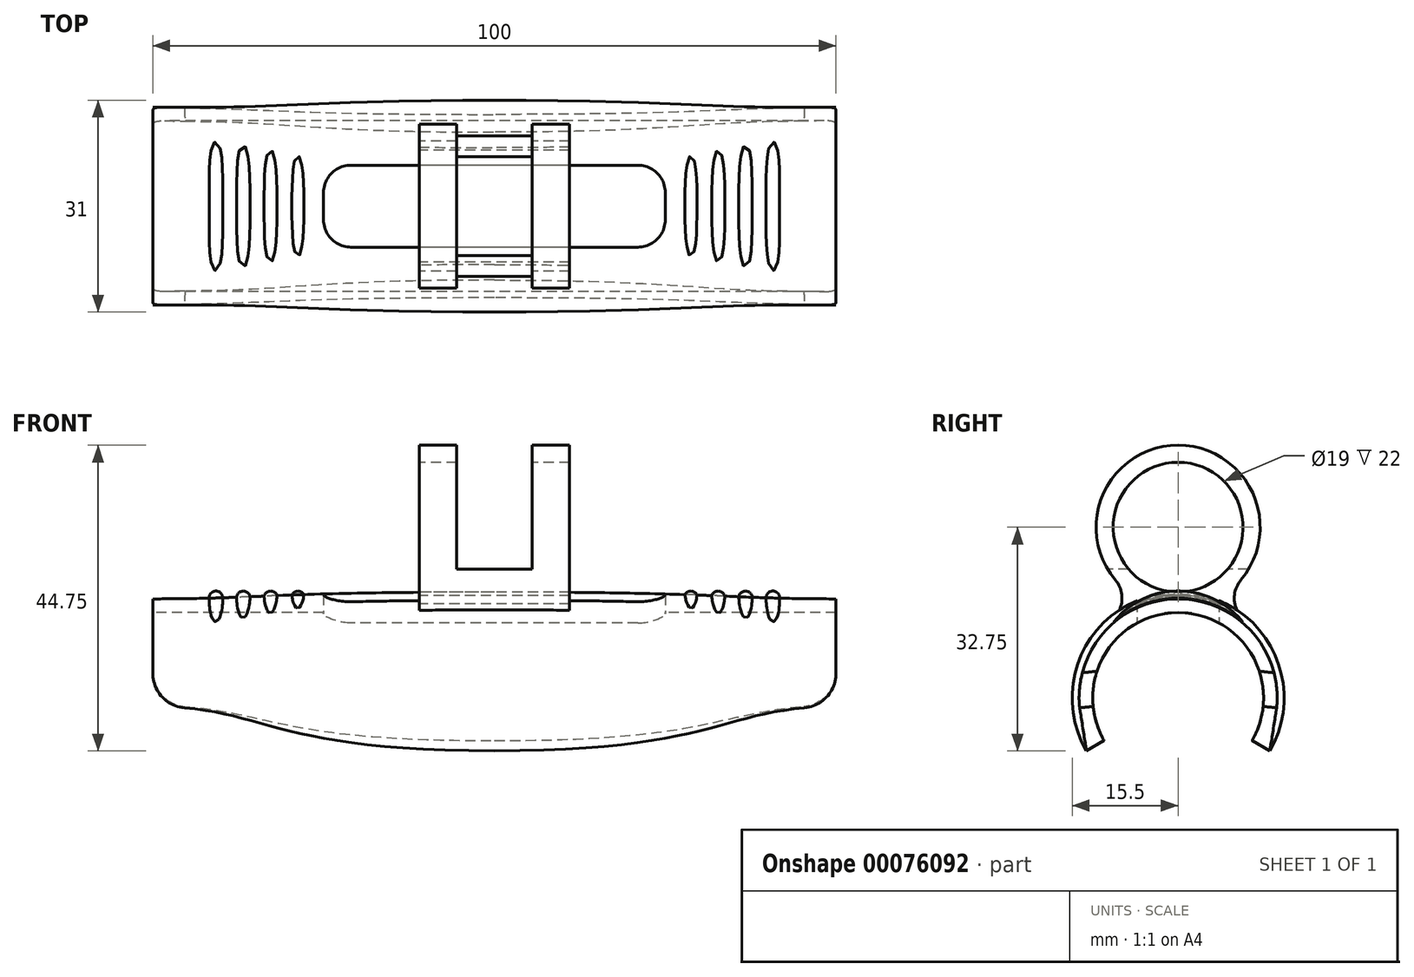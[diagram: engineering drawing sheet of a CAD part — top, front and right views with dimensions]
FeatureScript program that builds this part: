
annotation { "Feature Type Name" : "Feature", "Feature Type Description" : "" }
export const myFeature = defineFeature(function(context is Context, id is Id, definition is map)
    precondition{}
    {
        {
            var Q0;
            Q0=qCreatedBy(makeId("Right.planeOp"),FACE);
            var sketch = newSketch(context, id + "F0", { "sketchPlane" : qUnion([Q0])});
            skCircle(sketch, "E0", {"center": v(0, 0) * mm, "radius": 12.5 * mm});
            skSolve(sketch);
        }
        {
            var Q0;
            Q0=qCreatedBy(makeId("Right.planeOp"),FACE);
            var sketch = newSketch(context, id + "F1", { "sketchPlane" : qUnion([Q0])});
            skArc(sketch, "E1", {"start": v(10.83, -6.25) * mm, "mid": v(0, 12.5) * mm, "end": v(-10.83, -6.25) * mm});
            skArc(sketch, "E2.0", {"start": v(13.42, -7.75) * mm, "mid": v(0, 15.5) * mm, "end": v(-13.42, -7.75) * mm});
            skLineSegment(sketch, "E3", {"start": v(-10.83, -6.25) * mm, "end": v(-13.42, -7.75) * mm});
            skLineSegment(sketch, "E4", {"start": v(10.83, -6.25) * mm, "end": v(13.42, -7.75) * mm});
            skLineSegment(sketch, "E5", {"start": v(0, 20.1) * mm, "end": v(0, -26.2) * mm, "construction": true});
            skSolve(sketch);
        }
        {
            var Q0;
            Q0=qCreatedBy(makeId("Right.planeOp"),FACE);
            cPlane(context, id + "F2", {"entities" : qUnion([Q0]), "cplaneType" : CPlaneType.OFFSET, "offset" : 50 * mm, "width" : 152.4 * mm, "height" : 152.4 * mm});
        }
        {
            var Q0;
            Q0=qCreatedBy(id+"F2.planeOp",FACE);
            var sketch = newSketch(context, id + "F3", { "sketchPlane" : qUnion([Q0])});
            skArc(sketch, "E6", {"start": v(12.45, -1.09) * mm, "mid": v(0, 12.5) * mm, "end": v(-12.45, -1.09) * mm});
            skArc(sketch, "E7.0", {"start": v(14.44, -1.26) * mm, "mid": v(0, 14.5) * mm, "end": v(-14.44, -1.26) * mm});
            skLineSegment(sketch, "E8", {"start": v(-12.45, -1.09) * mm, "end": v(-14.44, -1.26) * mm});
            skLineSegment(sketch, "E9", {"start": v(12.45, -1.09) * mm, "end": v(14.44, -1.26) * mm});
            skSolve(sketch);
        }
        {
            var Q0;
            Q0=makeQuery(id+"F3.imprint","IMPRINT",FACE,{"disambiguationData":[TD([[makeQuery(id+"F3.imprint","IMPRINT",EDGE,{"derivedFrom":sQuery(id+"F3.wireOp",EDGE,"E6")}),-1.0]])]});
            var Q1;
            Q1 = qSketchRegion(id + "F1", true);
            loft(context, id + "F4", {"startCondition" : LoftEndDerivativeType.NORMAL_TO_PROFILE, "startMagnitude" : 1, "endCondition" : LoftEndDerivativeType.NORMAL_TO_PROFILE, "endMagnitude" : 2, "sheetProfilesArray" : [{ "sheetProfileEntities" : qUnion([Q0]) }, { "sheetProfileEntities" : qUnion([Q1]) }]});
        }
        {
            var Q0;
            Q0=makeQuery(id+"F4.opLoft","MID_CAP_EDGE",EDGE,{"disambiguationData":[OSD([sQuery(id+"F3.wireOp",EDGE,"E6"),sQuery(id+"F3.wireOp",EDGE,"E7.0"),sQuery(id+"F3.wireOp",EDGE,"E8")])],"capPos":0.0});
            var Q1;
            Q1=makeQuery(id+"F4.opLoft","MID_CAP_EDGE",EDGE,{"disambiguationData":[OSD([sQuery(id+"F3.wireOp",EDGE,"E6"),sQuery(id+"F3.wireOp",EDGE,"E7.0"),sQuery(id+"F3.wireOp",EDGE,"E9")])],"capPos":0.0});
            fillet(context, id + "F5", {"entities" : qUnion([Q0, Q1]), "radius" : 5.08 * mm, "tangentPropagation" : true, "allowEdgeOverflow" : false});
        }
        {
            var Q0;
            Q0=qCreatedBy(makeId("Top.planeOp"),FACE);
            var sketch = newSketch(context, id + "F6", { "sketchPlane" : qUnion([Q0])});
            skLineSegment(sketch, "E10.bottom", {"start": v(21, 6) * mm, "end": v(-25, 6) * mm});
            skLineSegment(sketch, "E10.top", {"start": v(21, -6) * mm, "end": v(-25, -6) * mm});
            skLineSegment(sketch, "E10.left", {"start": v(25, 2) * mm, "end": v(25, -2) * mm});
            skLineSegment(sketch, "E10.right", {"start": v(-25, 6) * mm, "end": v(-25, -6) * mm});
            skPoint(sketch, "E10.middle", {"position": v(0, 0) * mm});
            skPoint(sketch, "E11.visualSharp", {"position": v(25, 6) * mm});
            skArc(sketch, "E11.filletArc", {"start": v(25, 2) * mm, "mid": v(23.83, 4.83) * mm, "end": v(21, 6) * mm});
            skPoint(sketch, "E12.visualSharp", {"position": v(25, -6) * mm});
            skArc(sketch, "E12.filletArc", {"start": v(21, -6) * mm, "mid": v(23.83, -4.83) * mm, "end": v(25, -2) * mm});
            skSolve(sketch);
        }
        {
            var Q0;
            Q0=makeQuery(id+"F6.imprint","IMPRINT",FACE,{"disambiguationData":[TD([[makeQuery(id+"F6.imprint","IMPRINT",EDGE,{"derivedFrom":sQuery(id+"F6.wireOp",EDGE,"E10.bottom")}),1.0]])]});
            extrude(context, id + "F7", {"entities" : qUnion([Q0]), "operationType" : NewBodyOperationType.REMOVE, "depth" : 38.64 * mm});
        }
        {
            var Q0;
            Q0=qCreatedBy(makeId("Right.planeOp"),FACE);
            var sketch = newSketch(context, id + "F8", { "sketchPlane" : qUnion([Q0])});
            skArc(sketch, "E13", {"start": v(9.19, 17.28) * mm, "mid": v(0, 37) * mm, "end": v(-9.19, 17.28) * mm});
            skArc(sketch, "E14", {"start": v(9.68, 11.46) * mm, "mid": v(0, 15) * mm, "end": v(-9.68, 11.46) * mm});
            skArc(sketch, "E15", {"start": v(9.19, 17.28) * mm, "mid": v(8.23, 14.26) * mm, "end": v(9.68, 11.46) * mm});
            skArc(sketch, "E16", {"start": v(-9.68, 11.46) * mm, "mid": v(-8.23, 14.26) * mm, "end": v(-9.19, 17.28) * mm});
            skCircle(sketch, "E17", {"center": v(0, 25) * mm, "radius": 9.5 * mm});
            skSolve(sketch);
        }
        {
            var Q0;
            Q0=makeQuery(id+"F8.imprint","IMPRINT",FACE,{"disambiguationData":[TD([[makeQuery(id+"F8.imprint","IMPRINT",EDGE,{"derivedFrom":sQuery(id+"F8.wireOp",EDGE,"E13")}),1.0]])]});
            extrude(context, id + "F9", {"entities" : qUnion([Q0]), "operationType" : NewBodyOperationType.ADD, "depth" : 11 * mm});
        }
        {
            var Q0;
            Q0=qCreatedBy(makeId("Front.planeOp"),FACE);
            var sketch = newSketch(context, id + "F10", { "sketchPlane" : qUnion([Q0])});
            skCircle(sketch, "E18", {"center": v(28.75, 14.65) * mm, "radius": 1 * mm});
            skCircle(sketch, "E19.1.0.0", {"center": v(32.75, 14.65) * mm, "radius": 1 * mm});
            skCircle(sketch, "E19.2.0.0", {"center": v(36.75, 14.65) * mm, "radius": 1 * mm});
            skCircle(sketch, "E19.3.0.0", {"center": v(40.75, 14.65) * mm, "radius": 1 * mm});
            skLineSegment(sketch, "E19.direction1", {"start": v(28.75, 14.65) * mm, "end": v(32.75, 14.65) * mm, "construction": true});
            skLineSegment(sketch, "E20", {"start": v(22.18, 3.5) * mm, "end": v(46.53, 3.5) * mm, "construction": true});
            skSolve(sketch);
        }
        {
            var Q0;
            Q0=makeQuery(id+"F10.imprint","IMPRINT",FACE,{"disambiguationData":[TD([[makeQuery(id+"F10.imprint","IMPRINT",EDGE,{"derivedFrom":sQuery(id+"F10.wireOp",EDGE,"E19.3.0.0")}),1.0]])]});
            var Q1;
            Q1=makeQuery(id+"F10.imprint","IMPRINT",FACE,{"disambiguationData":[TD([[makeQuery(id+"F10.imprint","IMPRINT",EDGE,{"derivedFrom":sQuery(id+"F10.wireOp",EDGE,"E19.2.0.0")}),1.0]])]});
            var Q2;
            Q2=makeQuery(id+"F10.imprint","IMPRINT",FACE,{"disambiguationData":[TD([[makeQuery(id+"F10.imprint","IMPRINT",EDGE,{"derivedFrom":sQuery(id+"F10.wireOp",EDGE,"E19.1.0.0")}),1.0]])]});
            var Q3;
            Q3=makeQuery(id+"F10.imprint","IMPRINT",FACE,{"disambiguationData":[TD([[makeQuery(id+"F10.imprint","IMPRINT",EDGE,{"derivedFrom":sQuery(id+"F10.wireOp",EDGE,"E18")}),1.0]])]});
            var Q4;
            Q4=sQuery(id+"F10.wireOp",EDGE,"E20");
            revolve(context, id + "F11", {"operationType" : NewBodyOperationType.ADD, "entities" : qUnion([Q0, Q1, Q2, Q3]), "axis" : qUnion([Q4]), "revolveType" : RevolveType.FULL});
        }
        {
            var Q0;
            Q0=makeQuery(id+"F0.imprint","IMPRINT",FACE,{"disambiguationData":[TD([[makeQuery(id+"F0.imprint","IMPRINT",EDGE,{"derivedFrom":sQuery(id+"F0.wireOp",EDGE,"E0")}),1.0]])]});
            extrude(context, id + "F12", {"entities" : qUnion([Q0]), "operationType" : NewBodyOperationType.REMOVE, "endBound" : BoundingType.THROUGH_ALL, "depth" : 25.4 * mm});
        }
        {
            var Q0;
            Q0=makeQuery(id+"F4.opLoft","SWEPT_BODY",BODY,{"disambiguationData":[OSD([makeQuery(id+"F1.imprint","IMPRINT",FACE,{"disambiguationData":[TD([[makeQuery(id+"F1.imprint","IMPRINT",EDGE,{"derivedFrom":sQuery(id+"F1.wireOp",EDGE,"E1")}),-1.0]])]}),makeQuery(id+"F3.imprint","IMPRINT",FACE,{"disambiguationData":[TD([[makeQuery(id+"F3.imprint","IMPRINT",EDGE,{"derivedFrom":sQuery(id+"F3.wireOp",EDGE,"E6")}),-1.0]])]})])]});
            var Q1;
            Q1=qCreatedBy(makeId("Right.planeOp"),FACE);
            mirror(context, id + "F13", {"operationType" : NewBodyOperationType.ADD, "entities" : qUnion([Q0]), "mirrorPlane" : qUnion([Q1])});
        }
        {
            var Q0;
            Q0=qCreatedBy(makeId("Front.planeOp"),FACE);
            var sketch = newSketch(context, id + "F14", { "sketchPlane" : qUnion([Q0])});
            skLineSegment(sketch, "E21.bottom", {"start": v(-5.5, 18.84) * mm, "end": v(5.5, 18.84) * mm});
            skLineSegment(sketch, "E21.top", {"start": v(-5.5, 59.38) * mm, "end": v(5.5, 59.38) * mm});
            skLineSegment(sketch, "E21.left", {"start": v(-5.5, 18.84) * mm, "end": v(-5.5, 59.38) * mm});
            skLineSegment(sketch, "E21.right", {"start": v(5.5, 18.84) * mm, "end": v(5.5, 59.38) * mm});
            skPoint(sketch, "E21.middle", {"position": v(0, 39.1) * mm});
            skSolve(sketch);
        }
        {
            var Q0;
            Q0=makeQuery(id+"F14.imprint","IMPRINT",FACE,{"disambiguationData":[TD([[makeQuery(id+"F14.imprint","IMPRINT",EDGE,{"derivedFrom":sQuery(id+"F14.wireOp",EDGE,"E21.bottom")}),1.0]])]});
            extrude(context, id + "F15", {"entities" : qUnion([Q0]), "operationType" : NewBodyOperationType.REMOVE, "endBound" : BoundingType.SYMMETRIC, "oppositeDirection" : true, "depth" : 25.4 * mm});
        }
    });
